# Revit family: cpl_1.1_osc_PS_pn
name_source: partatom
category: Drzwi
revit_build: Autodesk Revit 2014 (Build: 20140709_2115(x64)
units: mm (PartAtom-declared; Revit-internal decimal feet)

## types (5) — shared parameters
Funkcja = Wewnętrzna
Hs = 2030 mm  [stored 6.6601 ft]
Model = CPL 1.1
Opis = Ościeżnica Porta System
Producent = PORTA KMI POLAND
URL = www.porta.com.pl
Wysokość brutto = 2060 mm
Zakończenie ściany = Wg obiektu nadrzędnego
wysokość = 2016 mm
zero-valued in all types: Szerokość, Wysokość

## per-type parameters (varying)
| type | Sb | Ss | Szerokość brutto | szerokość |
| pn 80 | 846 mm | 844 mm  [stored 2.76903 ft] | 880 mm | 800 mm  [stored 2.62467 ft] |
| pn 90 | 946 mm | 944 mm | 980 mm | 900 mm |
| pn 100 | 1046 mm | 1044 mm | 1080 mm | 1000 mm  [stored 3.28084 ft] |
| pn 70 | 746 mm | 744 mm | 780 mm | 700 mm |
| pn 60 | 646 mm | 644 mm | 680 mm | 600 mm  [stored 1.9685 ft] |

note: [stored X ft] marks values corroborated as IEEE doubles in the binary element streams (Revit-internal decimal feet)
